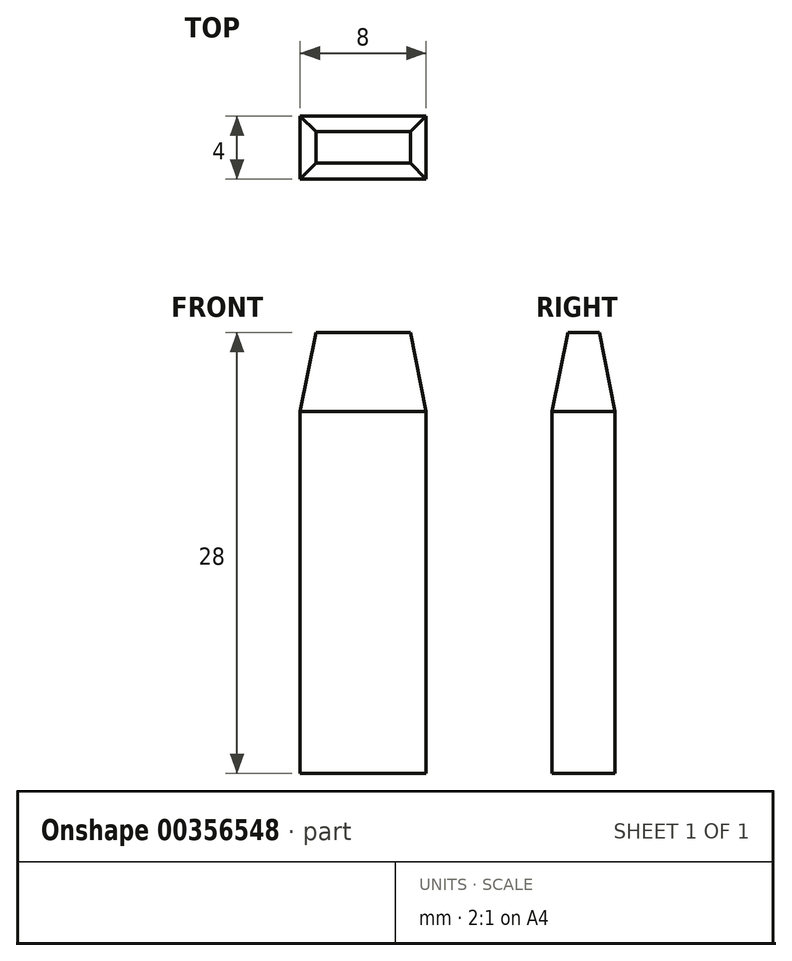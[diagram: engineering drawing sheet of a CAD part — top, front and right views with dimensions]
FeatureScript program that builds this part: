
annotation { "Feature Type Name" : "Feature", "Feature Type Description" : "" }
export const myFeature = defineFeature(function(context is Context, id is Id, definition is map)
    precondition{}
    {
        {
            var Q0;
            Q0=qCreatedBy(makeId("Top.planeOp"),FACE);
            var sketch = newSketch(context, id + "F0", { "sketchPlane" : qUnion([Q0])});
            skLineSegment(sketch, "E0.bottom", {"start": v(-2.78, 8.35) * mm, "end": v(5.22, 8.35) * mm});
            skLineSegment(sketch, "E0.top", {"start": v(-2.78, 4.35) * mm, "end": v(5.22, 4.35) * mm});
            skLineSegment(sketch, "E0.left", {"start": v(-2.78, 8.35) * mm, "end": v(-2.78, 4.35) * mm});
            skLineSegment(sketch, "E0.right", {"start": v(5.22, 8.35) * mm, "end": v(5.22, 4.35) * mm});
            skSolve(sketch);
        }
        {
            var Q0;
            Q0=makeQuery(id+"F0.imprint","IMPRINT",FACE,{"disambiguationData":[TD([[makeQuery(id+"F0.imprint","IMPRINT",EDGE,{"derivedFrom":sQuery(id+"F0.wireOp",EDGE,"E0.bottom")}),-1.0]])]});
            extrude(context, id + "F1", {"entities" : qUnion([Q0]), "depth" : 28 * mm});
        }
        {
            var Q0;
            Q0=makeQuery(id+"F1.opExtrude","CAP_EDGE",EDGE,{"disambiguationData":[OSD([sQuery(id+"F0.wireOp",EDGE,"E0.top")])],"isStart":false});
            var Q1;
            Q1=makeQuery(id+"F1.opExtrude","CAP_EDGE",EDGE,{"disambiguationData":[OSD([sQuery(id+"F0.wireOp",EDGE,"E0.bottom")])],"isStart":false});
            var Q2;
            Q2=makeQuery(id+"F1.opExtrude","CAP_EDGE",EDGE,{"disambiguationData":[OSD([sQuery(id+"F0.wireOp",EDGE,"E0.right")])],"isStart":false});
            var Q3;
            Q3=makeQuery(id+"F1.opExtrude","CAP_EDGE",EDGE,{"disambiguationData":[OSD([sQuery(id+"F0.wireOp",EDGE,"E0.left")])],"isStart":false});
            chamfer(context, id + "F2", {"entities" : qUnion([Q0, Q1, Q2, Q3]), "chamferType" : ChamferType.TWO_OFFSETS, "width1" : 1 * mm, "oppositeDirection" : false, "width2" : 5 * mm, "tangentPropagation" : true});
        }
    });
